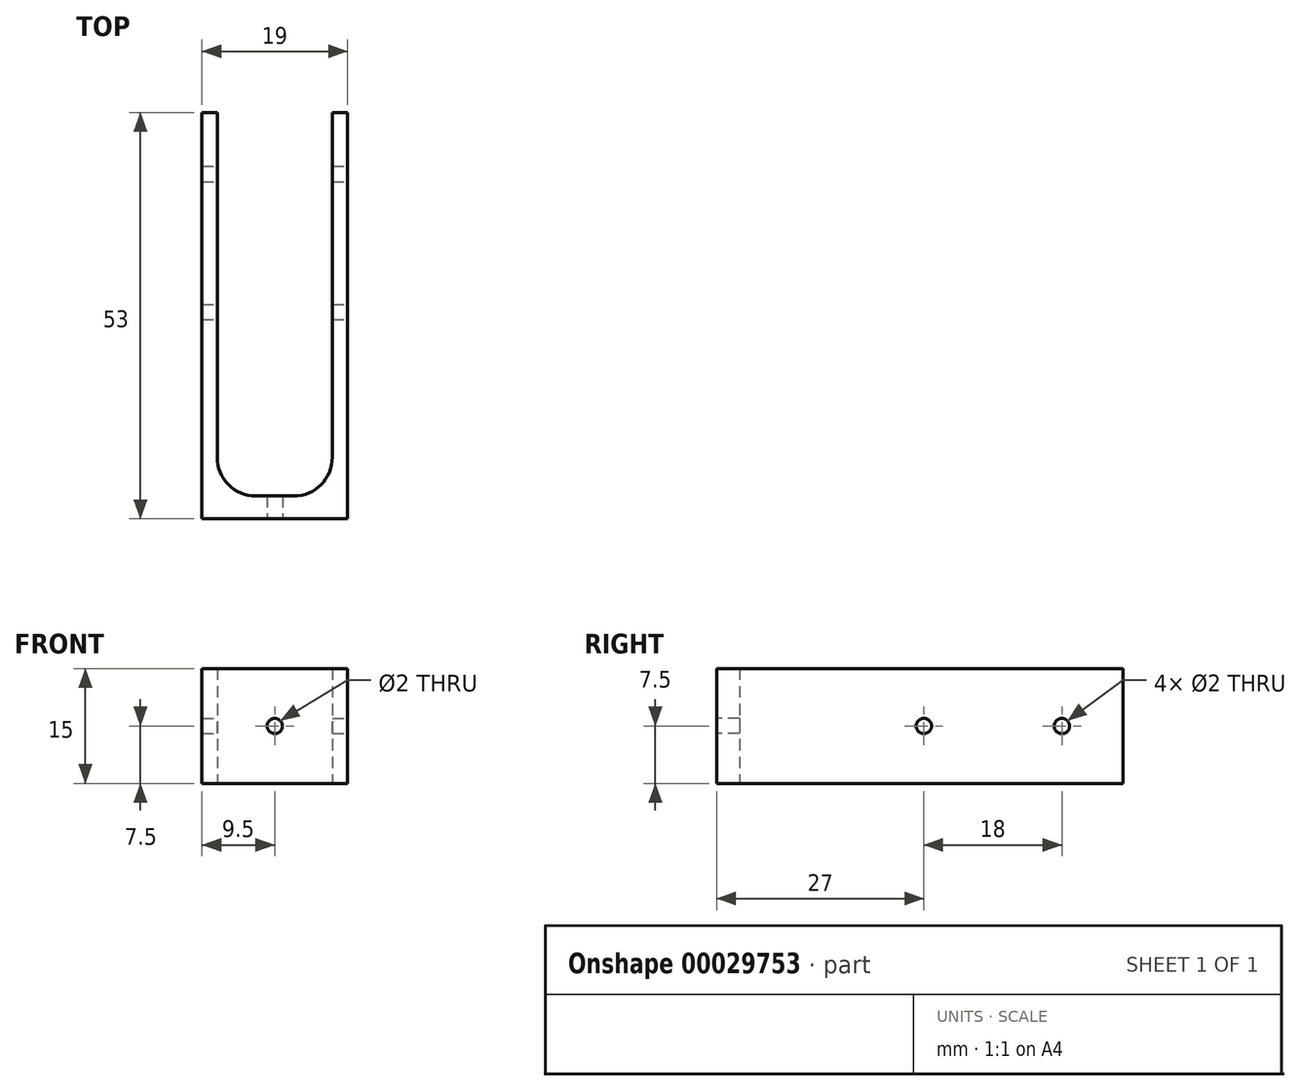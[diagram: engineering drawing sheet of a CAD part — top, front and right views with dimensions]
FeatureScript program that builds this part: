
annotation { "Feature Type Name" : "Feature", "Feature Type Description" : "" }
export const myFeature = defineFeature(function(context is Context, id is Id, definition is map)
    precondition{}
    {
        {
            var Q0;
            Q0=qCreatedBy(makeId("Top.planeOp"),FACE);
            var sketch = newSketch(context, id + "F0", { "sketchPlane" : qUnion([Q0])});
            skLineSegment(sketch, "E0.top", {"start": v(0, 53) * mm, "end": v(-2, 53) * mm});
            skLineSegment(sketch, "E0.left", {"start": v(0, 0) * mm, "end": v(0, 53) * mm});
            skLineSegment(sketch, "E0.right", {"start": v(-19, 0) * mm, "end": v(-19, 53) * mm});
            skLineSegment(sketch, "E1.top", {"start": v(-17, 3) * mm, "end": v(-2, 3) * mm});
            skLineSegment(sketch, "E1.left", {"start": v(-17, 53) * mm, "end": v(-17, 3) * mm});
            skLineSegment(sketch, "E1.right", {"start": v(-2, 53) * mm, "end": v(-2, 3) * mm});
            skLineSegment(sketch, "E2.trimOffspring", {"start": v(-17, 53) * mm, "end": v(-19, 53) * mm});
            skLineSegment(sketch, "E3", {"start": v(-19, 0) * mm, "end": v(0, 0) * mm});
            skPoint(sketch, "E4.end.orphan", {"position": v(12, 0) * mm});
            skPoint(sketch, "E5.end.orphan", {"position": v(-31, 0) * mm});
            skPoint(sketch, "E6.orphan", {"position": v(-21.5, 3) * mm});
            skPoint(sketch, "E7.start.orphan", {"position": v(-23.5, 53) * mm});
            skSolve(sketch);
        }
        {
            var Q0;
            Q0=makeQuery(id+"F0.imprint","IMPRINT",FACE,{"disambiguationData":[TD([[makeQuery(id+"F0.imprint","IMPRINT",EDGE,{"derivedFrom":sQuery(id+"F0.wireOp",EDGE,"E0.top")}),1.0]])]});
            extrude(context, id + "F1", {"entities" : qUnion([Q0]), "depth" : 15 * mm});
        }
        {
            var Q0;
            Q0=makeQuery(id+"F1.opExtrude","SWEPT_FACE",FACE,{"disambiguationData":[OSD([sQuery(id+"F0.wireOp",EDGE,"E0.left")])]});
            var sketch = newSketch(context, id + "F2", { "sketchPlane" : qUnion([Q0])});
            skCircle(sketch, "E8", {"center": v(27, 7.5) * mm, "radius": 1 * mm});
            skCircle(sketch, "E9", {"center": v(45, 7.5) * mm, "radius": 1 * mm});
            skSolve(sketch);
        }
        {
            var Q0;
            Q0=qSketchRegion(id+"F2",true);
            extrude(context, id + "F3", {"entities" : qUnion([Q0]), "operationType" : NewBodyOperationType.REMOVE, "oppositeDirection" : true, "depth" : 25 * mm});
        }
        {
            var Q0;
            Q0=makeQuery(id+"F1.opExtrude","SWEPT_FACE",FACE,{"disambiguationData":[OSD([sQuery(id+"F0.wireOp",EDGE,"E3"),sQuery(id+"F0.wireOp",EDGE,"E5"),sQuery(id+"F0.wireOp",EDGE,"KW2I9wrd-rldA-EDLi-8j01-u2Y36levhrCV")])]});
            var sketch = newSketch(context, id + "F4", { "sketchPlane" : qUnion([Q0])});
            skCircle(sketch, "E10", {"center": v(-9.5, 7.5) * mm, "radius": 1 * mm});
            skCircle(sketch, "E11", {"center": v(-25, 7.5) * mm, "radius": 1 * mm});
            skCircle(sketch, "E12", {"center": v(6, 7.5) * mm, "radius": 1 * mm});
            skLineSegment(sketch, "E13.0", {"start": v(12, 15) * mm, "end": v(12, 0) * mm});
            skCircle(sketch, "E14", {"center": v(-31, 7.5) * mm, "radius": 0.5 * mm});
            skCircle(sketch, "E15", {"center": v(12, 7.5) * mm, "radius": 0.5 * mm});
            skLineSegment(sketch, "E16.0", {"start": v(12, 15) * mm, "end": v(-31, 15) * mm});
            skSolve(sketch);
        }
        {
            var Q0;
            Q0=qSketchRegion(id+"F4",true);
            extrude(context, id + "F5", {"entities" : qUnion([Q0]), "operationType" : NewBodyOperationType.REMOVE, "oppositeDirection" : true, "depth" : 25 * mm});
        }
        {
            var Q0;
            Q0=makeQuery(id+"F1.opExtrude","SWEPT_EDGE",EDGE,{"disambiguationData":[OSD([sQuery(id+"F0.wireOp",EDGE,"E1.top"),sQuery(id+"F0.wireOp",EDGE,"E1.right")])]});
            var Q1;
            Q1=makeQuery(id+"F1.opExtrude","SWEPT_EDGE",EDGE,{"disambiguationData":[OSD([sQuery(id+"F0.wireOp",EDGE,"E1.top"),sQuery(id+"F0.wireOp",EDGE,"E1.left")])]});
            fillet(context, id + "F6", {"entities" : qUnion([Q0, Q1]), "radius" : 5 * mm, "tangentPropagation" : true, "allowEdgeOverflow" : false});
        }
    });
